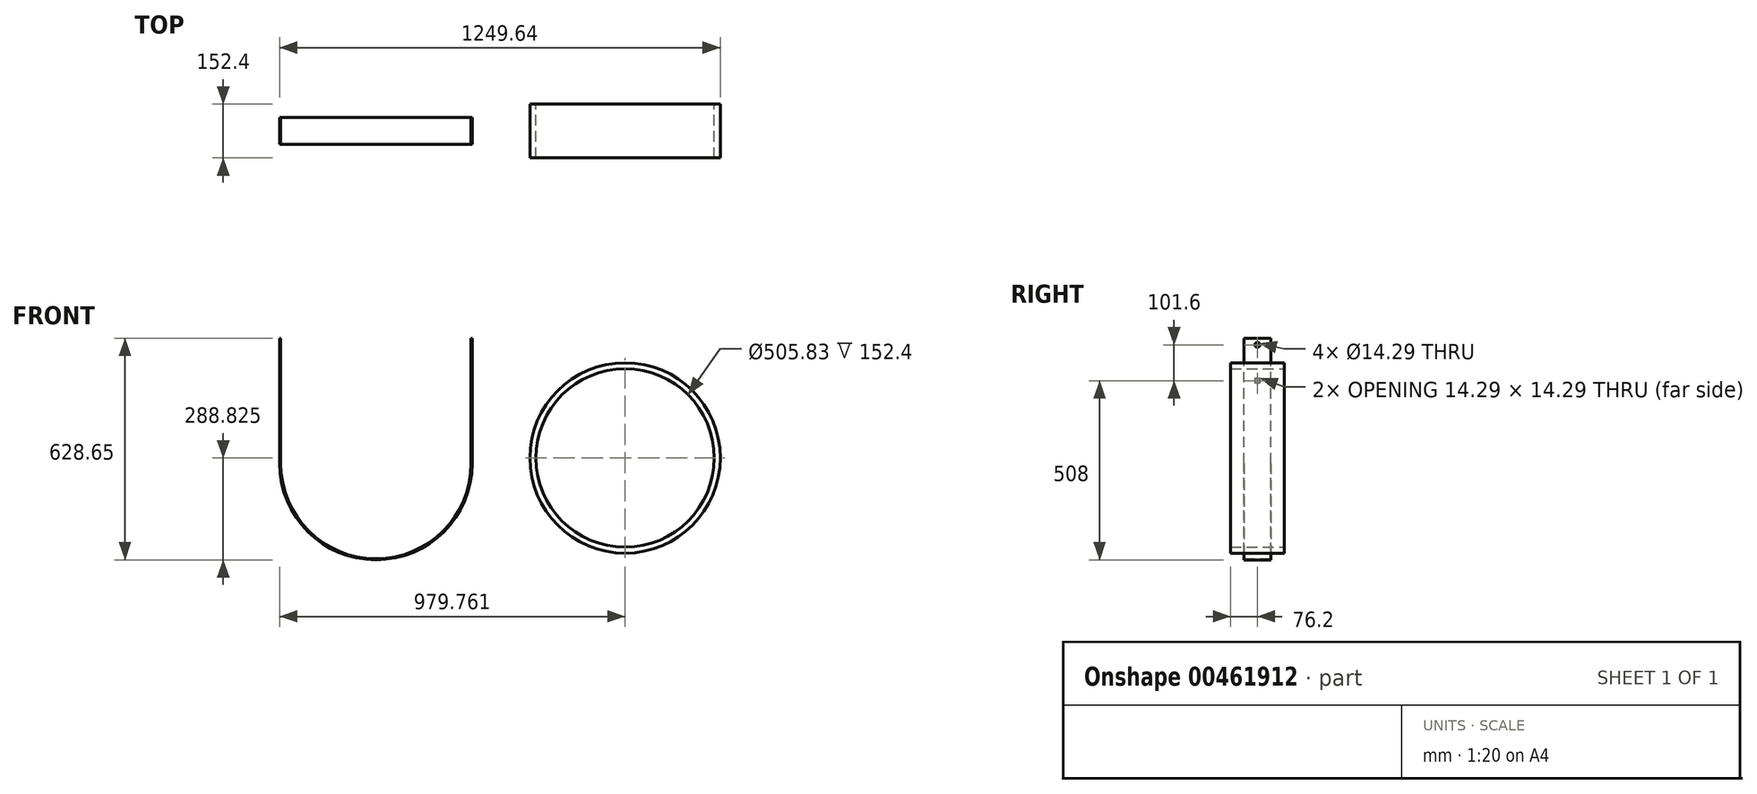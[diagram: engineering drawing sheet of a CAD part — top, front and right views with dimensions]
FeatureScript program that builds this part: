
annotation { "Feature Type Name" : "Feature", "Feature Type Description" : "" }
export const myFeature = defineFeature(function(context is Context, id is Id, definition is map)
    precondition{}
    {
        {
            var Q0;
            Q0=qCreatedBy(makeId("Front.planeOp"),FACE);
            var sketch = newSketch(context, id + "F0", { "sketchPlane" : qUnion([Q0])});
            skArc(sketch, "E0", {"start": v(-269.88, 0) * mm, "mid": v(0, -269.88) * mm, "end": v(269.88, 0) * mm});
            skArc(sketch, "E1", {"start": v(-273.05, 0) * mm, "mid": v(0, -273.05) * mm, "end": v(273.05, 0) * mm});
            skLineSegment(sketch, "E2", {"start": v(-269.88, 0) * mm, "end": v(-269.88, 355.6) * mm});
            skLineSegment(sketch, "E3", {"start": v(-269.88, 355.6) * mm, "end": v(-273.05, 355.6) * mm});
            skLineSegment(sketch, "E4", {"start": v(-273.05, 355.6) * mm, "end": v(-273.05, 0) * mm});
            skLineSegment(sketch, "E5", {"start": v(273.05, 0) * mm, "end": v(273.05, 355.6) * mm});
            skLineSegment(sketch, "E6", {"start": v(273.05, 355.6) * mm, "end": v(269.88, 355.6) * mm});
            skLineSegment(sketch, "E7", {"start": v(269.88, 355.6) * mm, "end": v(269.88, 0) * mm});
            skSolve(sketch);
        }
        {
            var Q0;
            Q0 = qSketchRegion(id + "F0", true);
            extrude(context, id + "F1", {"entities" : qUnion([Q0]), "endBound" : BoundingType.SYMMETRIC, "depth" : 76.2 * mm});
        }
        {
            var Q0;
            Q0=qCreatedBy(makeId("Right.planeOp"),FACE);
            var sketch = newSketch(context, id + "F2", { "sketchPlane" : qUnion([Q0])});
            skCircle(sketch, "E8", {"center": v(0, 336.55) * mm, "radius": 7.14 * mm});
            skCircle(sketch, "E9", {"center": v(0, 234.95) * mm, "radius": 7.14 * mm});
            skSolve(sketch);
        }
        {
            var Q0;
            Q0 = qSketchRegion(id + "F2", true);
            extrude(context, id + "F3", {"entities" : qUnion([Q0]), "operationType" : NewBodyOperationType.REMOVE, "endBound" : BoundingType.SYMMETRIC, "oppositeDirection" : true, "depth" : 635 * mm});
        }
        {
            var Q0;
            Q0=qCreatedBy(makeId("Front.planeOp"),FACE);
            var sketch = newSketch(context, id + "F4", { "sketchPlane" : qUnion([Q0])});
            skCircle(sketch, "E10", {"center": v(706.71, 15.78) * mm, "radius": 269.88 * mm});
            skCircle(sketch, "E11", {"center": v(706.71, 15.78) * mm, "radius": 252.91 * mm});
            skSolve(sketch);
        }
        {
            var Q0;
            Q0 = qSketchRegion(id + "F4", true);
            extrude(context, id + "F5", {"entities" : qUnion([Q0]), "endBound" : BoundingType.SYMMETRIC, "depth" : 152.4 * mm});
        }
    });
